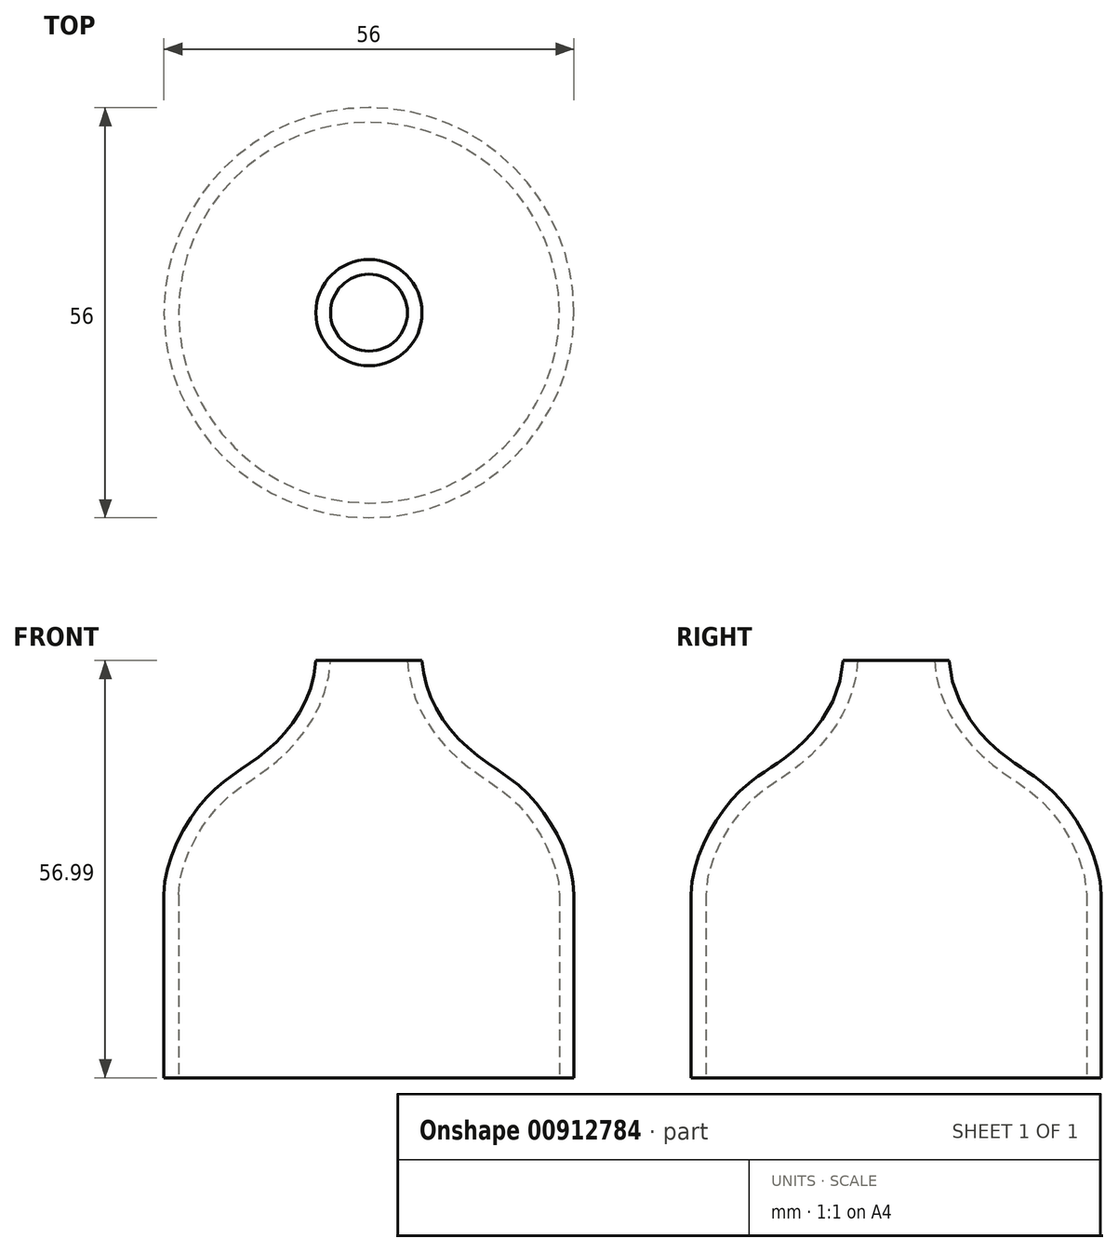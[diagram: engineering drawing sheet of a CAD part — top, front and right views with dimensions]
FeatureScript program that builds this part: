
annotation { "Feature Type Name" : "Feature", "Feature Type Description" : "" }
export const myFeature = defineFeature(function(context is Context, id is Id, definition is map)
    precondition{}
    {
        {
            var Q0;
            Q0=qCreatedBy(makeId("Front.planeOp"),FACE);
            var sketch = newSketch(context, id + "F0", { "sketchPlane" : qUnion([Q0])});
            skLineSegment(sketch, "E0", {"start": v(0, 0) * mm, "end": v(0, 57) * mm});
            skLineSegment(sketch, "E1", {"start": v(0, 57) * mm, "end": v(-7.25, 57) * mm});
            skLineSegment(sketch, "E2", {"start": v(0, 0) * mm, "end": v(-28, 0) * mm});
            skLineSegment(sketch, "E3", {"start": v(-28, 0) * mm, "end": v(-28, 25) * mm});
            skFitSpline(sketch, "E4", {"points": [v(-28, 25) * mm, v(-21.92, 38.54) * mm, v(-13.77, 44.85) * mm, v(-7.25, 57) * mm], "startDerivative": vector(0.18, 39.96) * mm, "endDerivative": vector(2.7, 45.86) * mm});
            skSolve(sketch);
        }
        {
            var Q0;
            Q0=makeQuery(id+"F0.imprint","IMPRINT",FACE,{"disambiguationData":[TD([[makeQuery(id+"F0.imprint","IMPRINT",EDGE,{"derivedFrom":sQuery(id+"F0.wireOp",EDGE,"E0")}),1.0]])]});
            var Q1;
            Q1=sQuery(id+"F0.wireOp",EDGE,"E0");
            revolve(context, id + "F1", {"surfaceOperationType" : NewSurfaceOperationType.NEW, "entities" : qUnion([Q0]), "axis" : qUnion([Q1]), "revolveType" : RevolveType.FULL});
        }
        {
            var Q0;
            Q0=makeQuery(id+"F1.opRevolve","SWEPT_FACE",FACE,{"disambiguationData":[OSD([sQuery(id+"F0.wireOp",EDGE,"E1")])]});
            var Q1;
            Q1=makeQuery(id+"F1.opRevolve","SWEPT_FACE",FACE,{"disambiguationData":[OSD([sQuery(id+"F0.wireOp",EDGE,"E2")])]});
            shell(context, id + "F2", {"entities" : qUnion([Q0, Q1]), "thickness" : 2 * mm});
        }
    });
